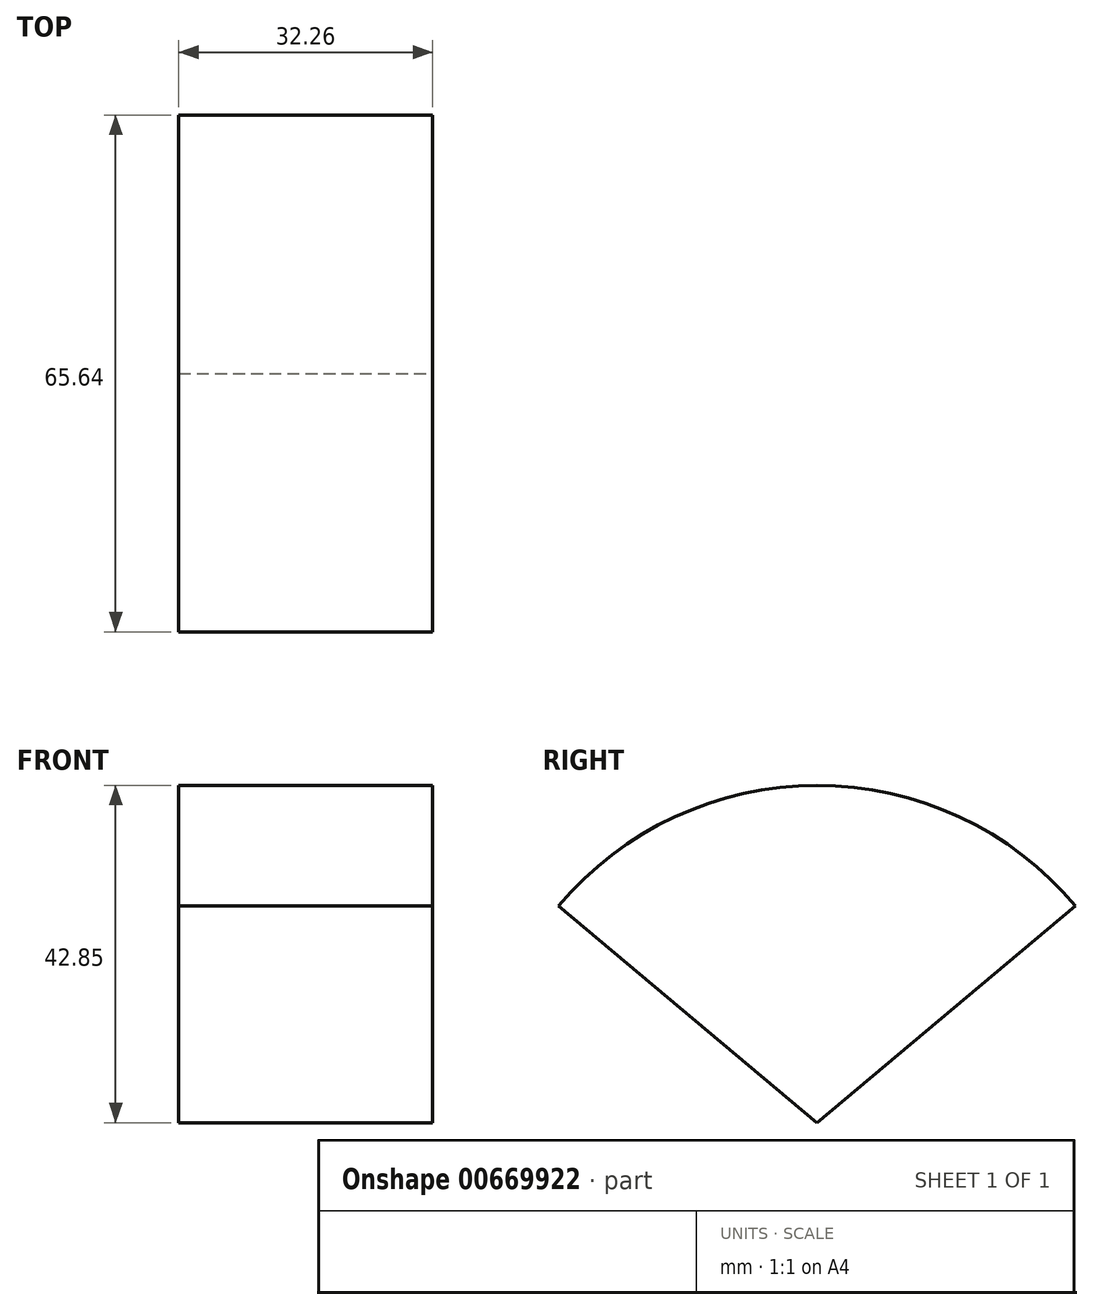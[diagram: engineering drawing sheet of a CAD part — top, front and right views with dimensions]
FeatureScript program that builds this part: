
annotation { "Feature Type Name" : "Feature", "Feature Type Description" : "" }
export const myFeature = defineFeature(function(context is Context, id is Id, definition is map)
    precondition{}
    {
        {
            var Q0;
            Q0=qCreatedBy(makeId("Front.planeOp"),FACE);
            var sketch = newSketch(context, id + "F0", { "sketchPlane" : qUnion([Q0])});
            skLineSegment(sketch, "E0.bottom", {"start": v(-75.06, 10.64) * mm, "end": v(-42.8, 10.64) * mm});
            skLineSegment(sketch, "E0.top", {"start": v(-75.06, 53.49) * mm, "end": v(-42.8, 53.49) * mm});
            skLineSegment(sketch, "E0.left", {"start": v(-75.06, 10.64) * mm, "end": v(-75.06, 53.49) * mm});
            skLineSegment(sketch, "E0.right", {"start": v(-42.8, 10.64) * mm, "end": v(-42.8, 53.49) * mm});
            skPoint(sketch, "E0.middle", {"position": v(-58.93, 32.06) * mm});
            skSolve(sketch);
        }
        {
            var Q0;
            Q0=makeQuery(id+"F0.imprint","IMPRINT",FACE,{"disambiguationData":[TD([[makeQuery(id+"F0.imprint","IMPRINT",EDGE,{"derivedFrom":sQuery(id+"F0.wireOp",EDGE,"E0.bottom")}),1.0]])]});
            var Q1;
            Q1=sQuery(id+"F0.wireOp",EDGE,"E0.bottom");
            revolve(context, id + "F1", {"entities" : qUnion([Q0]), "axis" : qUnion([Q1]), "revolveType" : RevolveType.SYMMETRIC, "angle" : 100 * degree});
        }
    });
